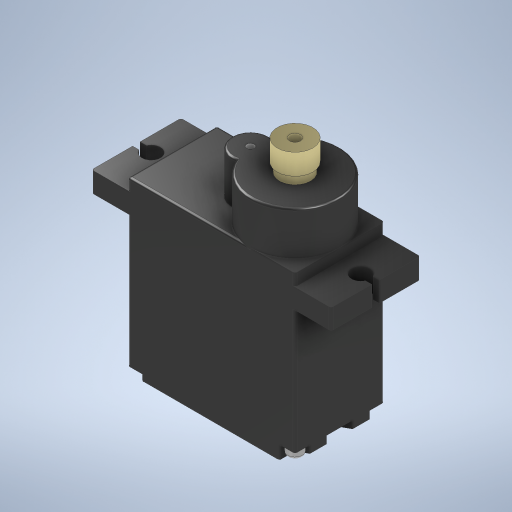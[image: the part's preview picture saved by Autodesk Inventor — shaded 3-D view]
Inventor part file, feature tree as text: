
AUTODESK INVENTOR PART (.ipt)
format: ipt  version: 2023 (Build 270158000, 158)  size: 586,752 bytes
history: native  units: mm
features: extrude x16, sketch x11, fillet x4, other x2, projected_geometry x2
ambient origin geometry x8: Origin, YZ Plane, XZ Plane, XY Plane, X Axis, Y Axis, Z Axis, Center Point
bodies: Body1 (feature_tree)
feature tree (35):
  other  "솔리드1"
  extrude  "돌출1"  Depth=22.5mm
  other  "작업 평면1"
  extrude  "돌출2"  Depth=12.0mm
  extrude  "돌출3"  Depth=23.0mm TaperAngle=0.0deg
  sketch  "스케치4"
  extrude  "돌출6"  [1 undecoded]
  extrude  "돌출7"  Depth=32.2mm
  fillet  "모깎기1"  Radius=12.0mm
  fillet  "모깎기2"  Radius=2.5mm
  sketch  "스케치5"
  extrude  "돌출8"  Depth=2.0mm
  extrude  "돌출9"  Depth=0.5mm
  extrude  "돌출10"  Depth=0.5mm
  extrude  "돌출11"  Depth=2.7mm TaperAngle=0.0deg
  fillet  "모깎기3"  Radius=1.0mm
  sketch  "스케치7"
  extrude  "돌출12"  Depth=1.5mm TaperAngle=0.0deg
  extrude  "돌출13"  Depth=5.0mm
  extrude  "돌출14"  Depth=6.0mm
  extrude  "돌출15"  Depth=5.0mm
  fillet  "모깎기4"  Radius=1.0mm
  extrude  "돌출16"  Depth=5.8mm TaperAngle=0.0deg
  sketch  "스케치12"
  sketch  "스케치14"
  extrude  "돌출18"  Depth=5.01mm TaperAngle=0.0deg
  extrude  "돌출19"  Depth=0.3mm
  sketch  "스케치15"
  sketch  "스케치16"
  sketch  "스케치1"
  sketch  "스케치2"
  sketch  "스케치3"
  projected_geometry  "투영된 루프1"
  projected_geometry  "투영된 루프2"
  sketch  "스케치6"
note: 1 required parameter value undecoded (feature->parameter linkage not recoverable at this tier; creation-order binding heuristic only, values carry confidence <= 0.55)
